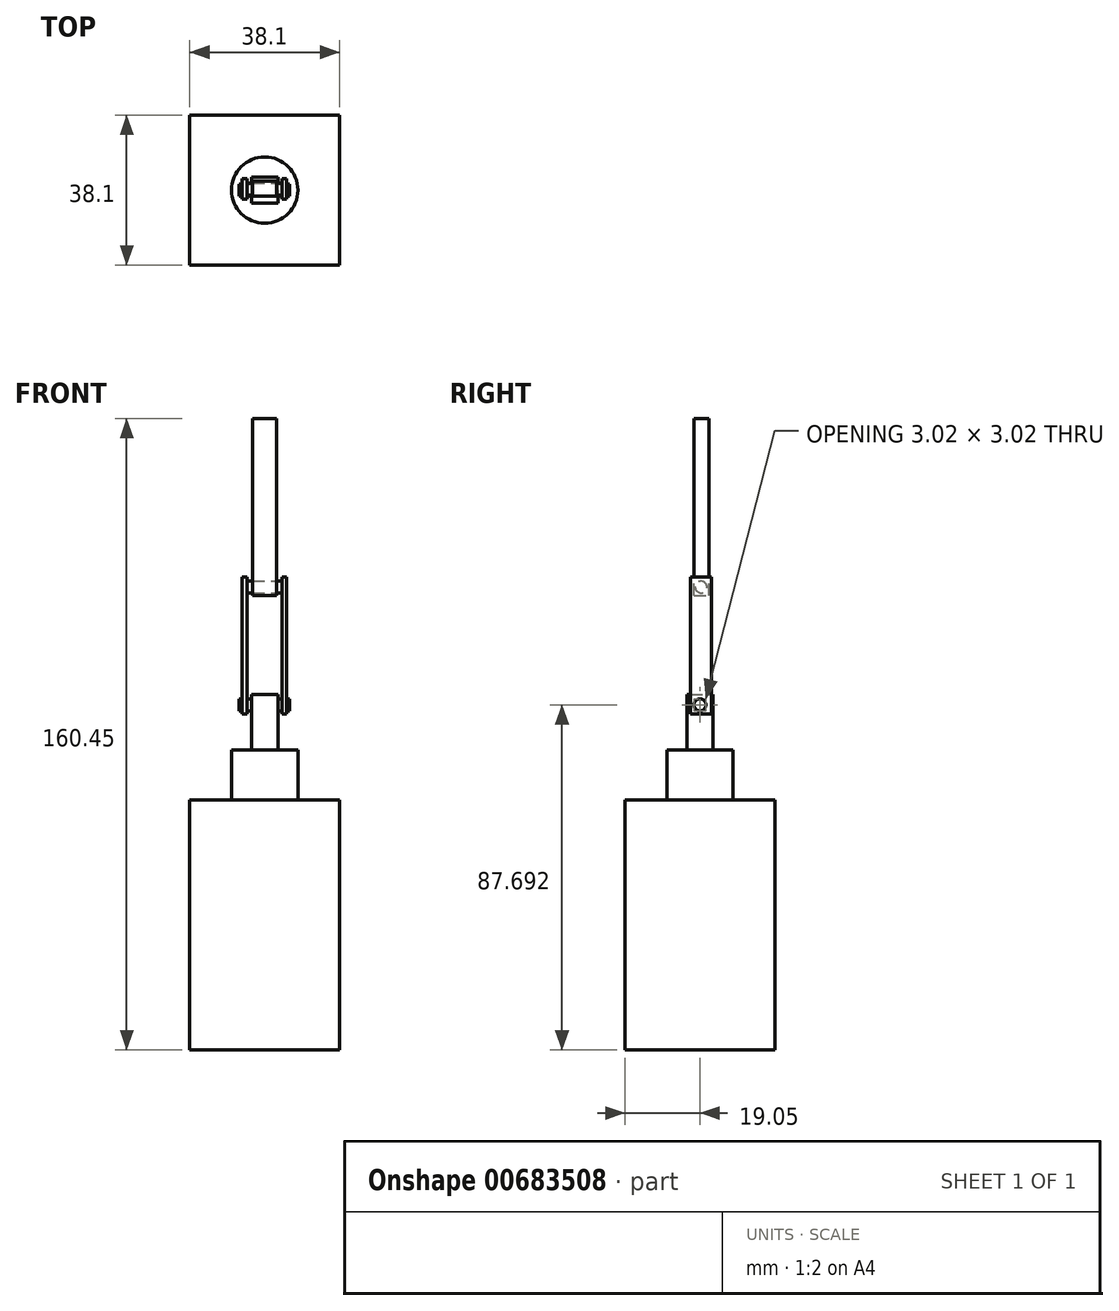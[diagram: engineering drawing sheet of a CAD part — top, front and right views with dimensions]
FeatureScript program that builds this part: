
annotation { "Feature Type Name" : "Feature", "Feature Type Description" : "" }
export const myFeature = defineFeature(function(context is Context, id is Id, definition is map)
    precondition{}
    {
        {
            var Q0;
            Q0=qCreatedBy(makeId("Top.planeOp"),FACE);
            var sketch = newSketch(context, id + "F0", { "sketchPlane" : qUnion([Q0])});
            skLineSegment(sketch, "E0.bottom", {"start": v(19.05, -19.05) * mm, "end": v(-19.05, -19.05) * mm});
            skLineSegment(sketch, "E0.top", {"start": v(19.05, 19.05) * mm, "end": v(-19.05, 19.05) * mm});
            skLineSegment(sketch, "E0.left", {"start": v(19.05, -19.05) * mm, "end": v(19.05, 19.05) * mm});
            skLineSegment(sketch, "E0.right", {"start": v(-19.05, -19.05) * mm, "end": v(-19.05, 19.05) * mm});
            skPoint(sketch, "E0.middle", {"position": v(0, 0) * mm});
            skSolve(sketch);
        }
        {
            var Q0;
            Q0 = qSketchRegion(id + "F0", true);
            extrude(context, id + "F1", {"entities" : qUnion([Q0]), "depth" : 63.5 * mm, "offsetDistance" : 25.4 * mm});
        }
        {
            var Q0;
            Q0=makeQuery(id+"F1.opExtrude","CAP_FACE",FACE,{"disambiguationData":[OSD([sQuery(id+"F0.wireOp",EDGE,"E0.bottom"),sQuery(id+"F0.wireOp",EDGE,"E0.top"),sQuery(id+"F0.wireOp",EDGE,"E0.left"),sQuery(id+"F0.wireOp",EDGE,"E0.right")])],"isStart":false});
            var sketch = newSketch(context, id + "F2", { "sketchPlane" : qUnion([Q0])});
            skCircle(sketch, "E1", {"center": v(0, 0) * mm, "radius": 8.43 * mm});
            skSolve(sketch);
        }
        {
            var Q0;
            Q0 = qSketchRegion(id + "F2", true);
            extrude(context, id + "F3", {"entities" : qUnion([Q0]), "operationType" : NewBodyOperationType.ADD, "depth" : 12.7 * mm, "offsetDistance" : 25.4 * mm});
        }
        {
            var Q0;
            Q0=makeQuery(id+"F3.opExtrude","CAP_FACE",FACE,{"disambiguationData":[OSD([sQuery(id+"F2.wireOp",EDGE,"E1")])],"isStart":false});
            var sketch = newSketch(context, id + "F4", { "sketchPlane" : qUnion([Q0])});
            skLineSegment(sketch, "E2.bottom", {"start": v(3.34, -3.25) * mm, "end": v(-3.34, -3.25) * mm});
            skLineSegment(sketch, "E2.top", {"start": v(3.34, 3.25) * mm, "end": v(-3.34, 3.25) * mm});
            skLineSegment(sketch, "E2.left", {"start": v(3.34, -3.25) * mm, "end": v(3.34, 3.25) * mm});
            skLineSegment(sketch, "E2.right", {"start": v(-3.34, -3.25) * mm, "end": v(-3.34, 3.25) * mm});
            skPoint(sketch, "E2.middle", {"position": v(0, 0) * mm});
            skSolve(sketch);
        }
        {
            var Q0;
            Q0 = qSketchRegion(id + "F4", true);
            extrude(context, id + "F5", {"entities" : qUnion([Q0]), "depth" : 14.16 * mm, "offsetDistance" : 25.4 * mm});
        }
        {
            var Q0;
            Q0=makeQuery(id+"F5.opExtrude","SWEPT_FACE",FACE,{"disambiguationData":[OSD([sQuery(id+"F4.wireOp",EDGE,"E2.right")])]});
            var sketch = newSketch(context, id + "F6", { "sketchPlane" : qUnion([Q0])});
            skCircle(sketch, "E3", {"center": v(0, 87.7) * mm, "radius": 1.51 * mm});
            skSolve(sketch);
        }
        {
            var Q0;
            Q0 = qSketchRegion(id + "F6", true);
            extrude(context, id + "F7", {"entities" : qUnion([Q0]), "operationType" : NewBodyOperationType.ADD, "depth" : 3.17 * mm, "offsetDistance" : 25.4 * mm, "hasSecondDirection" : true, "secondDirectionOppositeDirection" : true, "secondDirectionDepth" : 9.6 * mm});
        }
        {
            var Q0;
            Q0=qCreatedBy(makeId("Right.planeOp"),FACE);
            var sketch = newSketch(context, id + "F8", { "sketchPlane" : qUnion([Q0])});
            skLineSegment(sketch, "E4.bottom", {"start": v(-2.35, 85.35) * mm, "end": v(2.9, 85.35) * mm});
            skLineSegment(sketch, "E4.top", {"start": v(-2.35, 120.17) * mm, "end": v(2.9, 120.17) * mm});
            skLineSegment(sketch, "E4.left", {"start": v(-2.35, 85.35) * mm, "end": v(-2.35, 120.17) * mm});
            skLineSegment(sketch, "E4.right", {"start": v(2.9, 85.35) * mm, "end": v(2.9, 120.17) * mm});
            skSolve(sketch);
        }
        {
            var Q0;
            Q0 = qSketchRegion(id + "F8", true);
            extrude(context, id + "F9", {"entities" : qUnion([Q0]), "depth" : 5.54 * mm, "offsetDistance" : 25.4 * mm, "hasSecondDirection" : true, "secondDirectionOppositeDirection" : false, "secondDirectionDepth" : 4.35 * mm});
        }
        {
            var Q0;
            Q0 = qSketchRegion(id + "F8", true);
            extrude(context, id + "F10", {"entities" : qUnion([Q0]), "operationType" : NewBodyOperationType.ADD, "oppositeDirection" : true, "depth" : 5.8 * mm, "offsetDistance" : 25.4 * mm, "hasSecondDirection" : true, "secondDirectionOppositeDirection" : true, "secondDirectionDepth" : 4.44 * mm});
        }
        {
            var Q0;
            Q0=makeQuery(id+"F9.opExtrude","CAP_FACE",FACE,{"disambiguationData":[OSD([sQuery(id+"F8.wireOp",EDGE,"E4.bottom"),sQuery(id+"F8.wireOp",EDGE,"E4.top"),sQuery(id+"F8.wireOp",EDGE,"E4.left"),sQuery(id+"F8.wireOp",EDGE,"E4.right")])],"isStart":false});
            var sketch = newSketch(context, id + "F11", { "sketchPlane" : qUnion([Q0])});
            skCircle(sketch, "E5", {"center": v(0.28, 117.63) * mm, "radius": 1.5 * mm});
            skPoint(sketch, "E5.centerSnap0", {"position": v(0.28, 120.17) * mm});
            skSolve(sketch);
        }
        {
            var Q0;
            Q0 = qSketchRegion(id + "F11", true);
            extrude(context, id + "F12", {"entities" : qUnion([Q0]), "operationType" : NewBodyOperationType.ADD, "oppositeDirection" : true, "depth" : 10.12 * mm, "offsetDistance" : 25.4 * mm});
        }
        {
            var Q0;
            Q0=makeQuery(id+"F11.imprint","IMPRINT",FACE,{"disambiguationData":[TD([[makeQuery(id+"F11.imprint","IMPRINT",EDGE,{"derivedFrom":sQuery(id+"F11.wireOp",EDGE,"E5")}),-1.0]])]});
            var sketch = newSketch(context, id + "F13", { "sketchPlane" : qUnion([Q0])});
            skLineSegment(sketch, "E6.bottom", {"start": v(-1.52, 115.5) * mm, "end": v(2.3, 115.5) * mm});
            skLineSegment(sketch, "E6.top", {"start": v(-1.52, 160.45) * mm, "end": v(2.3, 160.45) * mm});
            skLineSegment(sketch, "E6.left", {"start": v(-1.52, 115.5) * mm, "end": v(-1.52, 160.45) * mm});
            skLineSegment(sketch, "E6.right", {"start": v(2.3, 115.5) * mm, "end": v(2.3, 160.45) * mm});
            skSolve(sketch);
        }
        {
            var Q0;
            Q0 = qSketchRegion(id + "F13", true);
            extrude(context, id + "F14", {"entities" : qUnion([Q0]), "oppositeDirection" : true, "depth" : 8.57 * mm, "offsetDistance" : 25.4 * mm, "hasSecondDirection" : true, "secondDirectionOppositeDirection" : true, "secondDirectionDepth" : 2.47 * mm});
        }
    });
